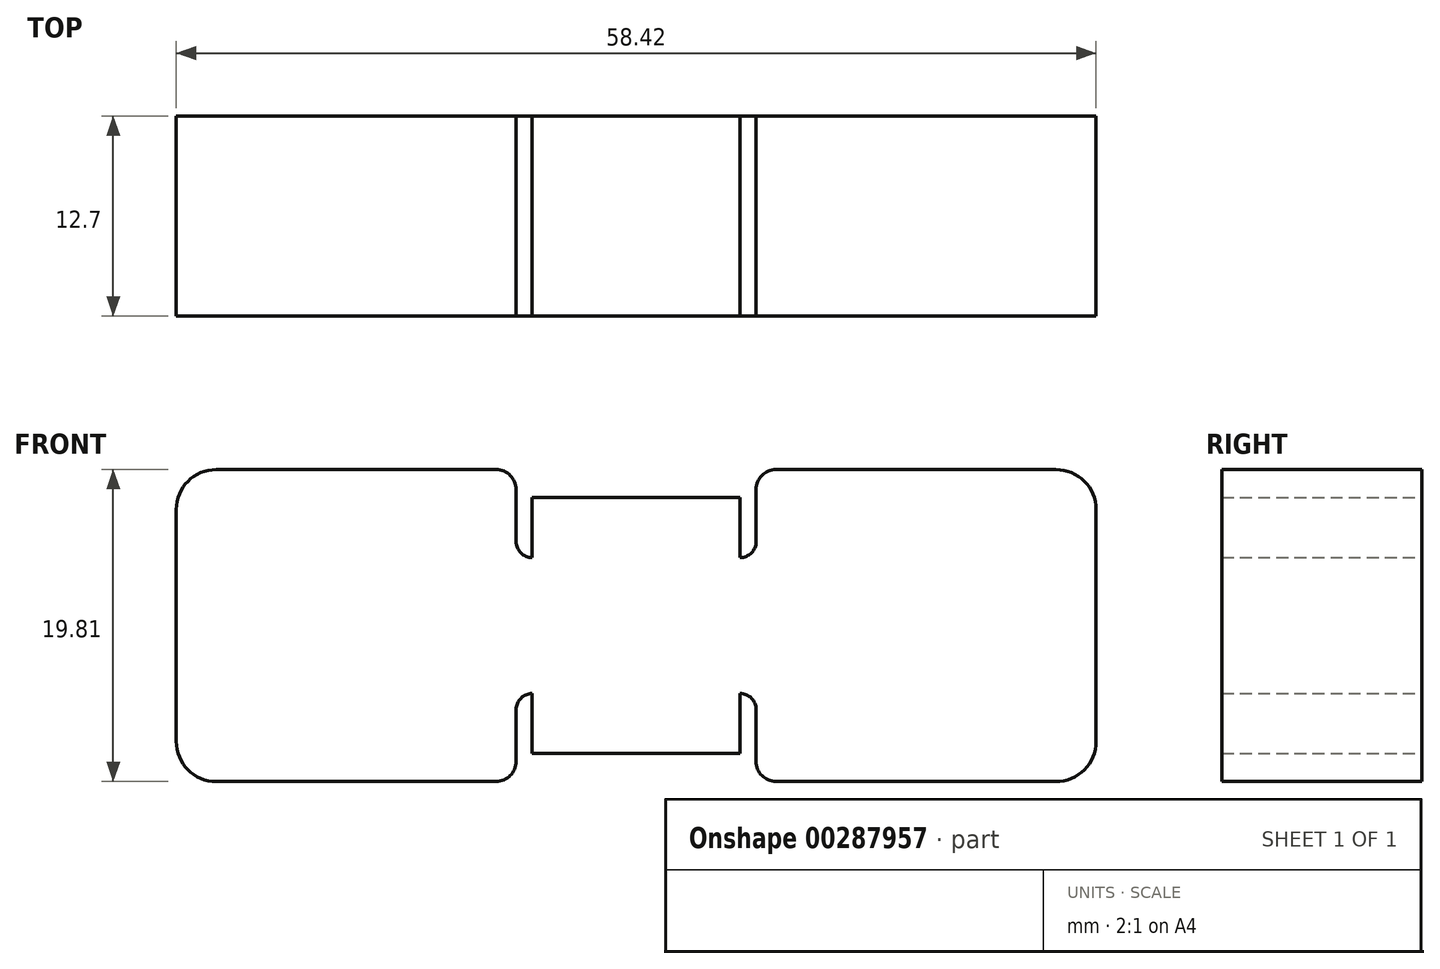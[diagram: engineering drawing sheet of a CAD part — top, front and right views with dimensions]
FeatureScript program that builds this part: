
annotation { "Feature Type Name" : "Feature", "Feature Type Description" : "" }
export const myFeature = defineFeature(function(context is Context, id is Id, definition is map)
    precondition{}
    {
        {
            var Q0;
            Q0=qCreatedBy(makeId("Front.planeOp"),FACE);
            var sketch = newSketch(context, id + "F0", { "sketchPlane" : qUnion([Q0])});
            skLineSegment(sketch, "E0", {"start": v(-17.54, 7.48) * mm, "end": v(-17.54, 0.11) * mm});
            skLineSegment(sketch, "E1", {"start": v(-17.54, 0.11) * mm, "end": v(11.67, 0.11) * mm});
            skLineSegment(sketch, "E2", {"start": v(11.67, 0.11) * mm, "end": v(11.67, 8.24) * mm});
            skLineSegment(sketch, "E3", {"start": v(11.67, 8.24) * mm, "end": v(5.06, 8.24) * mm});
            skLineSegment(sketch, "E4", {"start": v(5.06, 8.24) * mm, "end": v(5.06, 4.43) * mm});
            skLineSegment(sketch, "E5", {"start": v(5.06, 4.43) * mm, "end": v(5.06, 4.43) * mm});
            skLineSegment(sketch, "E6", {"start": v(4.05, 5.45) * mm, "end": v(4.05, 8.75) * mm});
            skLineSegment(sketch, "E7", {"start": v(2.78, 10.02) * mm, "end": v(-15, 10.02) * mm});
            skPoint(sketch, "E8.visualSharp", {"position": v(-17.54, 10.02) * mm});
            skArc(sketch, "E8.filletArc", {"start": v(-15, 10.02) * mm, "mid": v(-16.8, 9.27) * mm, "end": v(-17.54, 7.48) * mm});
            skPoint(sketch, "E9.visualSharp", {"position": v(4.05, 10.02) * mm});
            skArc(sketch, "E9.filletArc", {"start": v(4.05, 8.75) * mm, "mid": v(3.68, 9.65) * mm, "end": v(2.78, 10.02) * mm});
            skPoint(sketch, "E10.visualSharp", {"position": v(4.05, 4.43) * mm});
            skArc(sketch, "E10.filletArc", {"start": v(4.05, 5.45) * mm, "mid": v(4.35, 4.73) * mm, "end": v(5.06, 4.43) * mm});
            skLineSegment(sketch, "E11.MirrorCS", {"start": v(11.67, 8.24) * mm, "end": v(18.27, 8.24) * mm});
            skLineSegment(sketch, "E12.MirrorCS", {"start": v(40.88, 0.11) * mm, "end": v(11.67, 0.11) * mm});
            skLineSegment(sketch, "E13.MirrorCS", {"start": v(40.88, 7.48) * mm, "end": v(40.88, 0.11) * mm});
            skLineSegment(sketch, "E14.MirrorCS", {"start": v(20.56, 10.02) * mm, "end": v(38.34, 10.02) * mm});
            skArc(sketch, "E15.MirrorCS", {"start": v(38.34, 10.02) * mm, "mid": v(40.13, 9.27) * mm, "end": v(40.88, 7.48) * mm});
            skArc(sketch, "E16.MirrorCS", {"start": v(19.29, 8.75) * mm, "mid": v(19.66, 9.65) * mm, "end": v(20.56, 10.02) * mm});
            skLineSegment(sketch, "E17.MirrorCS", {"start": v(19.29, 5.45) * mm, "end": v(19.29, 8.75) * mm});
            skArc(sketch, "E18.MirrorCS", {"start": v(19.29, 5.45) * mm, "mid": v(19, 4.73) * mm, "end": v(18.27, 4.43) * mm});
            skLineSegment(sketch, "E19.MirrorCS", {"start": v(18.27, 8.24) * mm, "end": v(18.27, 4.43) * mm});
            skLineSegment(sketch, "E20.MirrorCS", {"start": v(2.78, -9.8) * mm, "end": v(-15, -9.8) * mm});
            skLineSegment(sketch, "E21.MirrorCS", {"start": v(20.56, -9.8) * mm, "end": v(38.34, -9.8) * mm});
            skArc(sketch, "E22.MirrorCS", {"start": v(19.29, -8.52) * mm, "mid": v(19.66, -9.42) * mm, "end": v(20.56, -9.8) * mm});
            skLineSegment(sketch, "E23.MirrorCS", {"start": v(19.29, -5.22) * mm, "end": v(19.29, -8.52) * mm});
            skArc(sketch, "E24.MirrorCS", {"start": v(19.29, -5.22) * mm, "mid": v(19, -4.5) * mm, "end": v(18.27, -4.2) * mm});
            skLineSegment(sketch, "E25.MirrorCS", {"start": v(18.27, -8.02) * mm, "end": v(18.27, -4.2) * mm});
            skLineSegment(sketch, "E26.MirrorCS", {"start": v(11.67, -8.02) * mm, "end": v(18.27, -8.02) * mm});
            skLineSegment(sketch, "E27.MirrorCS", {"start": v(11.67, -8.02) * mm, "end": v(5.06, -8.02) * mm});
            skLineSegment(sketch, "E28.MirrorCS", {"start": v(5.06, -8.02) * mm, "end": v(5.06, -4.2) * mm});
            skArc(sketch, "E29.MirrorCS", {"start": v(4.05, -5.22) * mm, "mid": v(4.35, -4.5) * mm, "end": v(5.06, -4.2) * mm});
            skLineSegment(sketch, "E30.MirrorCS", {"start": v(4.05, -5.22) * mm, "end": v(4.05, -8.52) * mm});
            skArc(sketch, "E31.MirrorCS", {"start": v(4.05, -8.52) * mm, "mid": v(3.68, -9.42) * mm, "end": v(2.78, -9.8) * mm});
            skArc(sketch, "E32.MirrorCS", {"start": v(-15, -9.8) * mm, "mid": v(-16.8, -9.05) * mm, "end": v(-17.54, -7.25) * mm});
            skLineSegment(sketch, "E33.MirrorCS", {"start": v(-17.54, -7.25) * mm, "end": v(-17.54, 0.11) * mm});
            skArc(sketch, "E34.MirrorCS", {"start": v(38.34, -9.8) * mm, "mid": v(40.13, -9.05) * mm, "end": v(40.88, -7.25) * mm});
            skLineSegment(sketch, "E35.MirrorCS", {"start": v(40.88, -7.25) * mm, "end": v(40.88, 0.11) * mm});
            skSolve(sketch);
        }
        {
            var Q0;
            Q0=makeQuery(id+"F0.imprint","IMPRINT",FACE,{"disambiguationData":[TD([[makeQuery(id+"F0.imprint","IMPRINT",EDGE,{"derivedFrom":sQuery(id+"F0.wireOp",EDGE,"E0")}),1.0]])]});
            var Q1;
            Q1=makeQuery(id+"F0.imprint","IMPRINT",FACE,{"disambiguationData":[TD([[makeQuery(id+"F0.imprint","IMPRINT",EDGE,{"derivedFrom":sQuery(id+"F0.wireOp",EDGE,"E2")}),-1.0]])]});
            var Q2;
            Q2=makeQuery(id+"F0.imprint","IMPRINT",FACE,{"disambiguationData":[TD([[makeQuery(id+"F0.imprint","IMPRINT",EDGE,{"derivedFrom":sQuery(id+"F0.wireOp",EDGE,"E1")}),-1.0]])]});
            extrude(context, id + "F1", {"entities" : qUnion([Q0, Q1, Q2]), "depth" : 12.7 * mm});
        }
    });
